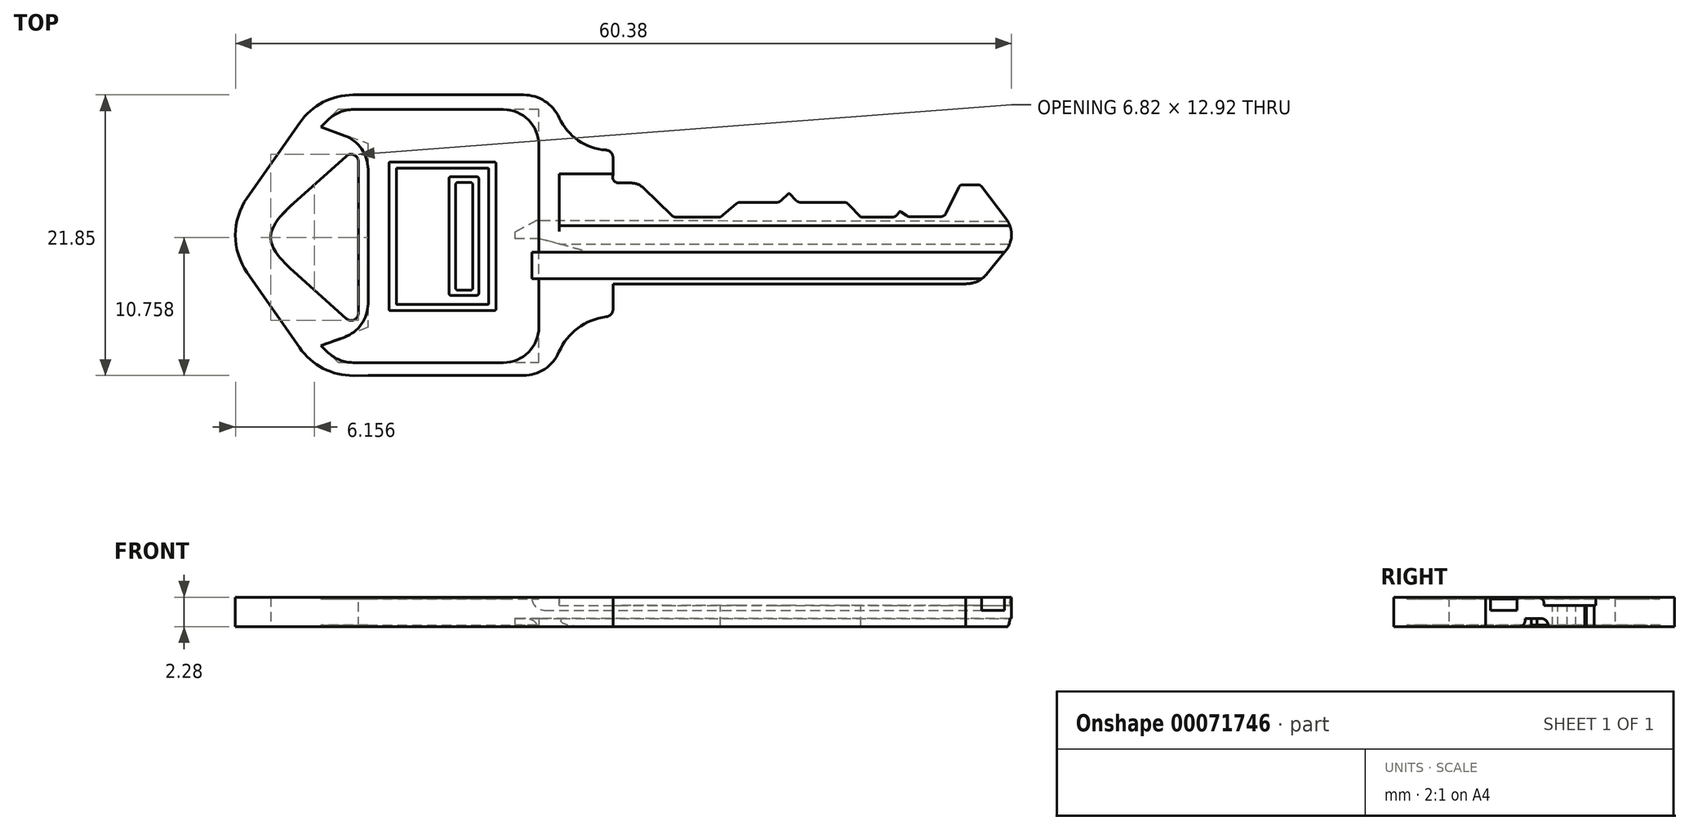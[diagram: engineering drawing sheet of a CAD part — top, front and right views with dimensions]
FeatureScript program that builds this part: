
annotation { "Feature Type Name" : "Feature", "Feature Type Description" : "" }
export const myFeature = defineFeature(function(context is Context, id is Id, definition is map)
    precondition{}
    {
        {
            var Q0;
            Q0=qCreatedBy(makeId("Top.planeOp"),FACE);
            var sketch = newSketch(context, id + "F0", { "sketchPlane" : qUnion([Q0])});
            skLineSegment(sketch, "E0.bottom", {"start": v(-49.06, 40.34) * mm, "end": v(-34.58, 40.34) * mm});
            skLineSegment(sketch, "E0.top", {"start": v(-49.06, 18.5) * mm, "end": v(-34.58, 18.5) * mm});
            skLineSegment(sketch, "E0.left", {"start": v(-49.06, 40.34) * mm, "end": v(-49.06, 18.5) * mm});
            skLineSegment(sketch, "E0.right", {"start": v(-34.58, 40.34) * mm, "end": v(-34.58, 18.5) * mm});
            skLineSegment(sketch, "E1.bottom", {"start": v(-34.58, 33.5) * mm, "end": v(-2.57, 33.5) * mm});
            skLineSegment(sketch, "E1.top", {"start": v(-34.58, 25.63) * mm, "end": v(-2.57, 25.63) * mm});
            skLineSegment(sketch, "E1.left", {"start": v(-34.58, 33.5) * mm, "end": v(-34.58, 25.63) * mm});
            skLineSegment(sketch, "E1.right", {"start": v(-2.57, 33.5) * mm, "end": v(-2.57, 25.63) * mm});
            skLineSegment(sketch, "E2.bottom", {"start": v(-34.58, 36.05) * mm, "end": v(-30, 36.05) * mm});
            skLineSegment(sketch, "E2.top", {"start": v(-34.58, 23.1) * mm, "end": v(-30, 23.1) * mm});
            skLineSegment(sketch, "E2.left", {"start": v(-34.58, 36.05) * mm, "end": v(-34.58, 23.1) * mm});
            skLineSegment(sketch, "E2.right", {"start": v(-30, 36.05) * mm, "end": v(-30, 23.1) * mm});
            skArc(sketch, "E3", {"start": v(-34.58, 40.34) * mm, "mid": v(-33.22, 37.2) * mm, "end": v(-30, 36.05) * mm});
            skArc(sketch, "E4", {"start": v(-30, 23.1) * mm, "mid": v(-33.25, 21.74) * mm, "end": v(-34.58, 18.5) * mm});
            skPoint(sketch, "E5", {"position": v(-30, 33.5) * mm});
            skPoint(sketch, "E6", {"position": v(-30, 25.63) * mm});
            skLineSegment(sketch, "E7", {"start": v(-49.06, 29.42) * mm, "end": v(-2.57, 29.42) * mm});
            skPoint(sketch, "E8", {"position": v(-30, 29.42) * mm});
            skLineSegment(sketch, "E9", {"start": v(-49.06, 40.34) * mm, "end": v(-52.87, 40.34) * mm});
            skLineSegment(sketch, "E10", {"start": v(-52.87, 40.34) * mm, "end": v(-60.5, 29.42) * mm});
            skLineSegment(sketch, "E11", {"start": v(-60.5, 29.42) * mm, "end": v(-52.87, 18.47) * mm});
            skLineSegment(sketch, "E12", {"start": v(-52.87, 18.47) * mm, "end": v(-49.06, 18.5) * mm});
            skLineSegment(sketch, "E13", {"start": v(-2.57, 33.5) * mm, "end": v(-1.57, 33.5) * mm});
            skLineSegment(sketch, "E14", {"start": v(-1.57, 33.5) * mm, "end": v(1.56, 29.42) * mm});
            skLineSegment(sketch, "E15", {"start": v(1.56, 29.42) * mm, "end": v(-1.57, 25.62) * mm});
            skLineSegment(sketch, "E16", {"start": v(-1.57, 25.62) * mm, "end": v(-2.57, 25.63) * mm});
            skSolve(sketch);
        }
        {
            var Q0;
            Q0=makeQuery(id+"F0.imprint","IMPRINT",FACE,{"disambiguationData":[TD([[makeQuery(id+"F0.imprint","IMPRINT",EDGE,{"derivedFrom":sQuery(id+"F0.wireOp",EDGE,"E1.bottom")}),-1.0]])]});
            var Q1;
            {var subQ0=sQuery(id+"F0.wireOp",EDGE,"E3");var subQ3=sQuery(id+"F0.wireOp",EDGE,"E2.bottom");var subQ5=makeQuery(id+"F0.imprint","INTERSECT",VERTEX,{"derivedFrom":[subQ3,subQ0]});Q1=makeQuery(id+"F0.imprint","IMPRINT",FACE,{"disambiguationData":[TD([[makeQuery(id+"F0.imprint","IMPRINT",EDGE,{"disambiguationData":[TD([[subQ5,1.0]])],"derivedFrom":subQ3}),1.0]])]});}
            var Q2;
            {var subQ4=sQuery(id+"F0.wireOp",EDGE,"E1.bottom");var subQ6=sQuery(id+"F0.wireOp",EDGE,"E2.left");var subQ7=makeQuery(id+"F0.imprint","INTERSECT",VERTEX,{"derivedFrom":[subQ4,subQ6]});Q2=makeQuery(id+"F0.imprint","IMPRINT",FACE,{"disambiguationData":[TD([[makeQuery(id+"F0.imprint","IMPRINT",EDGE,{"disambiguationData":[TD([[subQ7,-1.0]])],"derivedFrom":subQ4}),1.0]])]});}
            var Q3;
            {var subQ5=sQuery(id+"F0.wireOp",EDGE,"E2.top");Q3=makeQuery(id+"F0.imprint","IMPRINT",FACE,{"disambiguationData":[TD([[makeQuery(id+"F0.imprint","IMPRINT",EDGE,{"derivedFrom":subQ5}),1.0]])]});}
            var Q4;
            {var subQ0=sQuery(id+"F0.wireOp",EDGE,"E2.top");Q4=makeQuery(id+"F0.imprint","IMPRINT",FACE,{"disambiguationData":[TD([[makeQuery(id+"F0.imprint","IMPRINT",EDGE,{"derivedFrom":subQ0}),-1.0]])]});}
            var Q5;
            {var subQ0=sQuery(id+"F0.wireOp",EDGE,"3a7dfe4d-6823-4ebe-8630-0b1af203f991.3");Q5=makeQuery(id+"F0.imprint","IMPRINT",FACE,{"disambiguationData":[TD([[makeQuery(id+"F0.imprint","IMPRINT",EDGE,{"derivedFrom":subQ0}),1.0]])]});}
            var Q6;
            {var subQ0=sQuery(id+"F0.wireOp",EDGE,"E0.left");Q6=makeQuery(id+"F0.imprint","IMPRINT",FACE,{"disambiguationData":[TD([[makeQuery(id+"F0.imprint","IMPRINT",EDGE,{"derivedFrom":subQ0}),-1.0]])]});}
            var Q7;
            {var subQ4=sQuery(id+"F0.wireOp",EDGE,"E0.left");Q7=makeQuery(id+"F0.imprint","IMPRINT",FACE,{"disambiguationData":[TD([[makeQuery(id+"F0.imprint","IMPRINT",EDGE,{"derivedFrom":subQ4}),1.0]])]});}
            var Q8;
            {var subQ9=sQuery(id+"F0.wireOp",EDGE,"E0.top");Q8=makeQuery(id+"F0.imprint","IMPRINT",FACE,{"disambiguationData":[TD([[makeQuery(id+"F0.imprint","IMPRINT",EDGE,{"derivedFrom":subQ9}),1.0]])]});}
            var Q9;
            {var subQ0=sQuery(id+"F0.wireOp",EDGE,"E2.left");var subQ1=sQuery(id+"F0.wireOp",EDGE,"E1.top");var subQ2=makeQuery(id+"F0.imprint","INTERSECT",VERTEX,{"derivedFrom":[subQ1,subQ0]});Q9=makeQuery(id+"F0.imprint","IMPRINT",FACE,{"disambiguationData":[TD([[makeQuery(id+"F0.imprint","IMPRINT",EDGE,{"disambiguationData":[TD([[subQ2,-1.0]])],"derivedFrom":subQ1}),1.0]])]});}
            var Q10;
            {var subQ0=sQuery(id+"F0.wireOp",EDGE,"E1.right");var subQ1=sQuery(id+"F0.wireOp",EDGE,"E1.top");var subQ2=makeQuery(id+"F0.imprint","INTERSECT",VERTEX,{"derivedFrom":[subQ1,subQ0]});Q10=makeQuery(id+"F0.imprint","IMPRINT",FACE,{"disambiguationData":[TD([[makeQuery(id+"F0.imprint","IMPRINT",EDGE,{"disambiguationData":[TD([[subQ2,1.0]])],"derivedFrom":subQ1}),1.0]])]});}
            var Q11;
            {var subQ3=sQuery(id+"F0.wireOp",EDGE,"E13");Q11=makeQuery(id+"F0.imprint","IMPRINT",FACE,{"disambiguationData":[TD([[makeQuery(id+"F0.imprint","IMPRINT",EDGE,{"derivedFrom":subQ3}),-1.0]])]});}
            extrude(context, id + "F1", {"entities" : qUnion([Q0, Q1, Q2, Q3, Q4, Q5, Q6, Q7, Q8, Q9, Q10, Q11]), "endBound" : BoundingType.SYMMETRIC, "depth" : 2.3 * mm});
        }
        {
            var Q0;
            Q0=makeQuery(id+"F1.opExtrude","CAP_FACE",FACE,{"disambiguationData":[OSD([sQuery(id+"F0.wireOp",EDGE,"E0.bottom"),sQuery(id+"F0.wireOp",EDGE,"E0.top"),sQuery(id+"F0.wireOp",EDGE,"E1.bottom"),sQuery(id+"F0.wireOp",EDGE,"E1.top"),sQuery(id+"F0.wireOp",EDGE,"E1.right"),sQuery(id+"F0.wireOp",EDGE,"E2.right"),sQuery(id+"F0.wireOp",EDGE,"E3"),sQuery(id+"F0.wireOp",EDGE,"E4"),sQuery(id+"F0.wireOp",EDGE,"E9"),sQuery(id+"F0.wireOp",EDGE,"E10"),sQuery(id+"F0.wireOp",EDGE,"E11"),sQuery(id+"F0.wireOp",EDGE,"E12")])],"isStart":false});
            var sketch = newSketch(context, id + "F2", { "sketchPlane" : qUnion([Q0])});
            skLineSegment(sketch, "E17", {"start": v(-57.81, 29.25) * mm, "end": v(-49.81, 22.07) * mm});
            skLineSegment(sketch, "E18", {"start": v(-49.81, 22.07) * mm, "end": v(-49.81, 36.43) * mm});
            skLineSegment(sketch, "E19", {"start": v(-49.81, 36.43) * mm, "end": v(-57.81, 29.25) * mm});
            skPoint(sketch, "E20", {"position": v(-49.81, 29.25) * mm});
            skSolve(sketch);
        }
        {
            var Q0;
            Q0=makeQuery(id+"F1.opExtrude","SWEPT_EDGE",EDGE,{"disambiguationData":[OSD([sQuery(id+"F0.wireOp",EDGE,"E11"),sQuery(id+"F0.wireOp",EDGE,"E12")])]});
            var Q1;
            Q1=makeQuery(id+"F1.opExtrude","SWEPT_EDGE",EDGE,{"disambiguationData":[OSD([sQuery(id+"F0.wireOp",EDGE,"E9"),sQuery(id+"F0.wireOp",EDGE,"E10")])]});
            var Q2;
            Q2=makeQuery(id+"F1.opExtrude","SWEPT_EDGE",EDGE,{"disambiguationData":[OSD([sQuery(id+"F0.wireOp",EDGE,"E10"),sQuery(id+"F0.wireOp",EDGE,"E11")])]});
            fillet(context, id + "F3", {"entities" : qUnion([Q0, Q1, Q2]), "radius" : 5.08 * mm, "tangentPropagation" : true, "allowEdgeOverflow" : false});
        }
        {
            var Q0;
            Q0=makeQuery(id+"F1.opExtrude","SWEPT_EDGE",EDGE,{"disambiguationData":[OSD([sQuery(id+"F0.wireOp",EDGE,"E0.bottom"),sQuery(id+"F0.wireOp",EDGE,"E0.right"),sQuery(id+"F0.wireOp",EDGE,"E3")])]});
            var Q1;
            Q1=makeQuery(id+"F1.opExtrude","SWEPT_EDGE",EDGE,{"disambiguationData":[OSD([sQuery(id+"F0.wireOp",EDGE,"E0.top"),sQuery(id+"F0.wireOp",EDGE,"E0.right"),sQuery(id+"F0.wireOp",EDGE,"E4")])]});
            fillet(context, id + "F4", {"entities" : qUnion([Q0, Q1]), "radius" : 3.05 * mm, "tangentPropagation" : true, "allowEdgeOverflow" : false});
        }
        {
            var Q0;
            Q0=makeQuery(id+"F1.opExtrude","SWEPT_EDGE",EDGE,{"disambiguationData":[OSD([sQuery(id+"F0.wireOp",EDGE,"E2.bottom"),sQuery(id+"F0.wireOp",EDGE,"E2.right"),sQuery(id+"F0.wireOp",EDGE,"E3")])]});
            var Q1;
            Q1=makeQuery(id+"F1.opExtrude","SWEPT_EDGE",EDGE,{"disambiguationData":[OSD([sQuery(id+"F0.wireOp",EDGE,"E2.top"),sQuery(id+"F0.wireOp",EDGE,"E2.right"),sQuery(id+"F0.wireOp",EDGE,"E4")])]});
            fillet(context, id + "F5", {"entities" : qUnion([Q0, Q1]), "radius" : 0.6 * mm, "tangentPropagation" : true, "allowEdgeOverflow" : false});
        }
        {
            var Q0;
            Q0=makeQuery(id+"F2.imprint","IMPRINT",FACE,{"disambiguationData":[TD([[makeQuery(id+"F2.imprint","IMPRINT",EDGE,{"derivedFrom":sQuery(id+"F2.wireOp",EDGE,"E17")}),1.0]])]});
            extrude(context, id + "F6", {"entities" : qUnion([Q0]), "operationType" : NewBodyOperationType.REMOVE, "endBound" : BoundingType.THROUGH_ALL, "oppositeDirection" : true, "depth" : 9.1 * mm});
        }
        {
            var Q0;
            Q0=makeQuery(id+"F6.boolean.opBoolean","COPY",EDGE,{"derivedFrom":makeQuery(id+"F6.opExtrude","SWEPT_EDGE",EDGE,{"disambiguationData":[OSD([sQuery(id+"F2.wireOp",EDGE,"E17"),sQuery(id+"F2.wireOp",EDGE,"E18")])]})});
            var Q1;
            Q1=makeQuery(id+"F6.boolean.opBoolean","COPY",EDGE,{"derivedFrom":makeQuery(id+"F6.opExtrude","SWEPT_EDGE",EDGE,{"disambiguationData":[OSD([sQuery(id+"F2.wireOp",EDGE,"E18"),sQuery(id+"F2.wireOp",EDGE,"E19")])]})});
            fillet(context, id + "F7", {"entities" : qUnion([Q0, Q1]), "radius" : 0.58 * mm, "tangentPropagation" : true, "allowEdgeOverflow" : false});
        }
        {
            var Q0;
            Q0=makeQuery(id+"F6.boolean.opBoolean","COPY",EDGE,{"derivedFrom":makeQuery(id+"F6.opExtrude","SWEPT_EDGE",EDGE,{"disambiguationData":[OSD([sQuery(id+"F2.wireOp",EDGE,"E17"),sQuery(id+"F2.wireOp",EDGE,"E19")])]})});
            fillet(context, id + "F8", {"entities" : qUnion([Q0]), "radius" : 3.55 * mm, "tangentPropagation" : true, "rho" : .6, "crossSection" : FilletCrossSection.CONIC, "allowEdgeOverflow" : false});
        }
        {
            var Q0;
            Q0=makeQuery(id+"F2.imprint","IMPRINT",FACE,{"disambiguationData":[TD([[makeQuery(id+"F2.imprint","IMPRINT",EDGE,{"derivedFrom":sQuery(id+"F2.wireOp",EDGE,"E17")}),-1.0]])]});
            var sketch = newSketch(context, id + "F9", { "sketchPlane" : qUnion([Q0])});
            skLineSegment(sketch, "E21", {"start": v(-49.06, 29.42) * mm, "end": v(-49.06, 36.47) * mm});
            skLineSegment(sketch, "E22", {"start": v(-49.06, 36.47) * mm, "end": v(-52.73, 37.84) * mm});
            skLineSegment(sketch, "E23", {"start": v(-52.73, 37.84) * mm, "end": v(-51.36, 39.2) * mm});
            skLineSegment(sketch, "E24", {"start": v(-51.36, 39.2) * mm, "end": v(-35.77, 39.2) * mm});
            skLineSegment(sketch, "E25", {"start": v(-35.77, 39.2) * mm, "end": v(-35.77, 19.5) * mm});
            skLineSegment(sketch, "E26", {"start": v(-35.77, 19.5) * mm, "end": v(-51.36, 19.5) * mm});
            skLineSegment(sketch, "E27", {"start": v(-51.36, 19.5) * mm, "end": v(-52.73, 20.83) * mm});
            skLineSegment(sketch, "E28", {"start": v(-52.73, 20.83) * mm, "end": v(-49.06, 22.13) * mm});
            skLineSegment(sketch, "E29", {"start": v(-49.06, 22.13) * mm, "end": v(-49.06, 29.42) * mm});
            skLineSegment(sketch, "E30.bottom", {"start": v(-36.33, 28.08) * mm, "end": v(0.92, 28.08) * mm});
            skLineSegment(sketch, "E30.top", {"start": v(-36.33, 26.03) * mm, "end": v(0.92, 26.03) * mm});
            skLineSegment(sketch, "E30.left", {"start": v(-36.33, 28.08) * mm, "end": v(-36.33, 26.03) * mm});
            skLineSegment(sketch, "E30.right", {"start": v(0.92, 28.08) * mm, "end": v(0.92, 26.03) * mm});
            skLineSegment(sketch, "E31.bottom", {"start": v(-34.2, 34.2) * mm, "end": v(3.04, 34.2) * mm});
            skLineSegment(sketch, "E31.top", {"start": v(-34.2, 30.17) * mm, "end": v(3.04, 30.17) * mm});
            skLineSegment(sketch, "E31.left", {"start": v(-34.2, 34.2) * mm, "end": v(-34.2, 30.17) * mm});
            skLineSegment(sketch, "E31.right", {"start": v(3.04, 34.2) * mm, "end": v(3.04, 30.17) * mm});
            skSolve(sketch);
        }
        {
            var Q0;
            Q0=makeQuery(id+"F1.opExtrude","CAP_FACE",FACE,{"disambiguationData":[OSD([sQuery(id+"F0.wireOp",EDGE,"E0.bottom"),sQuery(id+"F0.wireOp",EDGE,"E0.top"),sQuery(id+"F0.wireOp",EDGE,"E1.bottom"),sQuery(id+"F0.wireOp",EDGE,"E1.top"),sQuery(id+"F0.wireOp",EDGE,"E2.right"),sQuery(id+"F0.wireOp",EDGE,"E3"),sQuery(id+"F0.wireOp",EDGE,"E4"),sQuery(id+"F0.wireOp",EDGE,"E9"),sQuery(id+"F0.wireOp",EDGE,"E10"),sQuery(id+"F0.wireOp",EDGE,"E11"),sQuery(id+"F0.wireOp",EDGE,"E12"),sQuery(id+"F0.wireOp",EDGE,"E13"),sQuery(id+"F0.wireOp",EDGE,"E14"),sQuery(id+"F0.wireOp",EDGE,"E15"),sQuery(id+"F0.wireOp",EDGE,"E16")])],"isStart":true});
            var sketch = newSketch(context, id + "F10", { "sketchPlane" : qUnion([Q0])});
            skLineSegment(sketch, "E32", {"start": v(-49.08, -22.24) * mm, "end": v(-49.08, -19.13) * mm});
            skLineSegment(sketch, "E33", {"start": v(-49.08, -22.24) * mm, "end": v(-52.74, -20.87) * mm});
            skLineSegment(sketch, "E34", {"start": v(-52.74, -20.87) * mm, "end": v(-51.38, -19.51) * mm});
            skLineSegment(sketch, "E35", {"start": v(-51.38, -19.51) * mm, "end": v(-35.78, -19.51) * mm});
            skLineSegment(sketch, "E36", {"start": v(-35.78, -19.51) * mm, "end": v(-35.78, -39.2) * mm});
            skLineSegment(sketch, "E37", {"start": v(-35.78, -39.2) * mm, "end": v(-51.38, -39.2) * mm});
            skLineSegment(sketch, "E38", {"start": v(-51.38, -39.2) * mm, "end": v(-52.74, -37.88) * mm});
            skLineSegment(sketch, "E39", {"start": v(-52.74, -37.88) * mm, "end": v(-49.08, -36.58) * mm});
            skLineSegment(sketch, "E40", {"start": v(-49.08, -36.58) * mm, "end": v(-49.08, -19.13) * mm});
            skLineSegment(sketch, "E41", {"start": v(-35.64, -30.58) * mm, "end": v(-35.92, -30.58) * mm});
            skLineSegment(sketch, "E42", {"start": v(-35.92, -30.58) * mm, "end": v(-37.64, -29.65) * mm});
            skLineSegment(sketch, "E43", {"start": v(-37.64, -29.65) * mm, "end": v(-37.64, -29.19) * mm});
            skLineSegment(sketch, "E44", {"start": v(-37.64, -29.19) * mm, "end": v(-35.78, -29.19) * mm});
            skLineSegment(sketch, "E45", {"start": v(-35.78, -29.19) * mm, "end": v(-34.07, -28.7) * mm});
            skLineSegment(sketch, "E46", {"start": v(-34.07, -28.7) * mm, "end": v(2.33, -28.7) * mm});
            skLineSegment(sketch, "E47", {"start": v(2.33, -28.7) * mm, "end": v(2.33, -30.5) * mm});
            skLineSegment(sketch, "E48", {"start": v(2.33, -30.5) * mm, "end": v(-35.64, -30.58) * mm});
            skSolve(sketch);
        }
        {
            var Q0;
            Q0=makeQuery(id+"F9.imprint","IMPRINT",FACE,{"disambiguationData":[TD([[makeQuery(id+"F9.imprint","IMPRINT",EDGE,{"derivedFrom":sQuery(id+"F9.wireOp",EDGE,"E21")}),-1.0]])]});
            var Q1;
            {var subQ4=sQuery(id+"F10.wireOp",EDGE,"E37");Q1=makeQuery(id+"F10.imprint","IMPRINT",FACE,{"disambiguationData":[TD([[makeQuery(id+"F10.imprint","IMPRINT",EDGE,{"derivedFrom":subQ4}),-1.0]])]});}
            var Q2;
            {var subQ0=sQuery(id+"F10.wireOp",EDGE,"E33");Q2=makeQuery(id+"F10.imprint","IMPRINT",FACE,{"disambiguationData":[TD([[makeQuery(id+"F10.imprint","IMPRINT",EDGE,{"derivedFrom":subQ0}),-1.0]])]});}
            extrude(context, id + "F11", {"entities" : qUnion([Q0, Q1, Q2]), "operationType" : NewBodyOperationType.REMOVE, "endBound" : BoundingType.SYMMETRIC, "oppositeDirection" : true, "depth" : 0.25 * mm});
        }
        {
            var Q0;
            Q0=makeQuery(id+"F11.boolean.opBoolean","COPY",EDGE,{"derivedFrom":makeQuery(id+"F11.opExtrude","SWEPT_EDGE",EDGE,{"disambiguationData":[OSD([sQuery(id+"F9.wireOp",EDGE,"E28"),sQuery(id+"F9.wireOp",EDGE,"E29")])]})});
            var Q1;
            Q1=makeQuery(id+"F11.boolean.opBoolean","COPY",EDGE,{"derivedFrom":makeQuery(id+"F11.opExtrude","SWEPT_EDGE",EDGE,{"disambiguationData":[OSD([sQuery(id+"F9.wireOp",EDGE,"E21"),sQuery(id+"F9.wireOp",EDGE,"E22")])]})});
            var Q2;
            Q2=makeQuery(id+"F11.boolean.opBoolean","COPY",EDGE,{"derivedFrom":makeQuery(id+"F11.opExtrude","SWEPT_EDGE",EDGE,{"disambiguationData":[OSD([sQuery(id+"F9.wireOp",EDGE,"E25"),sQuery(id+"F9.wireOp",EDGE,"E26")])]})});
            var Q3;
            Q3=makeQuery(id+"F11.boolean.opBoolean","COPY",EDGE,{"derivedFrom":makeQuery(id+"F11.opExtrude","SWEPT_EDGE",EDGE,{"disambiguationData":[OSD([sQuery(id+"F9.wireOp",EDGE,"E24"),sQuery(id+"F9.wireOp",EDGE,"E25")])]})});
            var Q4;
            Q4=makeQuery(id+"F11.boolean.opBoolean","COPY",EDGE,{"derivedFrom":makeQuery(id+"F11.opExtrude","SWEPT_EDGE",EDGE,{"disambiguationData":[OSD([sQuery(id+"F9.wireOp",EDGE,"E26"),sQuery(id+"F9.wireOp",EDGE,"E27")])]})});
            var Q5;
            Q5=makeQuery(id+"F11.boolean.opBoolean","COPY",EDGE,{"derivedFrom":makeQuery(id+"F11.opExtrude","SWEPT_EDGE",EDGE,{"disambiguationData":[OSD([sQuery(id+"F9.wireOp",EDGE,"E23"),sQuery(id+"F9.wireOp",EDGE,"E24")])]})});
            fillet(context, id + "F12", {"entities" : qUnion([Q0, Q1, Q2, Q3, Q4, Q5]), "radius" : 2.8 * mm, "tangentPropagation" : true, "allowEdgeOverflow" : false});
        }
        {
            var Q0;
            Q0=makeQuery(id+"F1.opExtrude","SWEPT_EDGE",EDGE,{"disambiguationData":[OSD([sQuery(id+"F0.wireOp",EDGE,"E15"),sQuery(id+"F0.wireOp",EDGE,"E16")])]});
            var Q1;
            Q1=makeQuery(id+"F1.opExtrude","SWEPT_EDGE",EDGE,{"disambiguationData":[OSD([sQuery(id+"F0.wireOp",EDGE,"E14"),sQuery(id+"F0.wireOp",EDGE,"E15")])]});
            fillet(context, id + "F13", {"entities" : qUnion([Q0, Q1]), "radius" : 2.05 * mm, "tangentPropagation" : true, "allowEdgeOverflow" : false});
        }
        {
            var Q0;
            {var subQ1=sQuery(id+"F9.wireOp",EDGE,"E31.top");Q0=makeQuery(id+"F9.imprint","IMPRINT",FACE,{"disambiguationData":[TD([[makeQuery(id+"F9.imprint","IMPRINT",EDGE,{"derivedFrom":subQ1}),1.0]])]});}
            extrude(context, id + "F14", {"entities" : qUnion([Q0]), "operationType" : NewBodyOperationType.REMOVE, "endBound" : BoundingType.SYMMETRIC, "oppositeDirection" : true, "depth" : 1.27 * mm});
        }
        {
            var Q0;
            {var subQ4=sQuery(id+"F10.wireOp",EDGE,"E42");Q0=makeQuery(id+"F10.imprint","IMPRINT",FACE,{"disambiguationData":[TD([[makeQuery(id+"F10.imprint","IMPRINT",EDGE,{"derivedFrom":subQ4}),-1.0]])]});}
            var Q1;
            {var subQ1=sQuery(id+"F10.wireOp",EDGE,"E45");Q1=makeQuery(id+"F10.imprint","IMPRINT",FACE,{"disambiguationData":[TD([[makeQuery(id+"F10.imprint","IMPRINT",EDGE,{"derivedFrom":subQ1}),-1.0]])]});}
            extrude(context, id + "F15", {"entities" : qUnion([Q0, Q1]), "operationType" : NewBodyOperationType.REMOVE, "endBound" : BoundingType.SYMMETRIC, "oppositeDirection" : true, "depth" : 1.27 * mm});
        }
        {
            var Q0;
            {var subQ0=sQuery(id+"F9.wireOp",EDGE,"E30.bottom");var subQ1=sQuery(id+"F9.wireOp",EDGE,"E25");var subQ2=makeQuery(id+"F9.imprint","INTERSECT",VERTEX,{"derivedFrom":[subQ1,subQ0]});Q0=makeQuery(id+"F9.imprint","IMPRINT",FACE,{"disambiguationData":[TD([[makeQuery(id+"F9.imprint","IMPRINT",EDGE,{"disambiguationData":[TD([[subQ2,-1.0]])],"derivedFrom":subQ1}),1.0]])]});}
            var Q1;
            {var subQ5=sQuery(id+"F9.wireOp",EDGE,"E30.left");Q1=makeQuery(id+"F9.imprint","IMPRINT",FACE,{"disambiguationData":[TD([[makeQuery(id+"F9.imprint","IMPRINT",EDGE,{"derivedFrom":subQ5}),1.0]])]});}
            var Q2;
            {var subQ0=sQuery(id+"F9.wireOp",EDGE,"E30.right");Q2=makeQuery(id+"F9.imprint","IMPRINT",FACE,{"disambiguationData":[TD([[makeQuery(id+"F9.imprint","IMPRINT",EDGE,{"derivedFrom":subQ0}),-1.0]])]});}
            extrude(context, id + "F16", {"entities" : qUnion([Q0, Q1, Q2]), "operationType" : NewBodyOperationType.REMOVE, "endBound" : BoundingType.SYMMETRIC, "oppositeDirection" : true, "depth" : 2.03 * mm});
        }
        {
            var Q0;
            Q0=makeQuery(id+"F16.boolean.opBoolean","COPY",EDGE,{"derivedFrom":makeQuery(id+"F16.opExtrude","CAP_EDGE",EDGE,{"disambiguationData":[OSD([sQuery(id+"F9.wireOp",EDGE,"E30.left")])],"isStart":false})});
            fillet(context, id + "F17", {"entities" : qUnion([Q0]), "radius" : 0.99 * mm, "tangentPropagation" : true, "allowEdgeOverflow" : false});
        }
        {
            var Q0;
            Q0=makeQuery(id+"F14.boolean.opBoolean","INTERSECT",EDGE,{"derivedFrom":[makeQuery(id+"F1.opExtrude","CAP_FACE",FACE,{"disambiguationData":[OSD([sQuery(id+"F0.wireOp",EDGE,"E0.bottom"),sQuery(id+"F0.wireOp",EDGE,"E0.top"),sQuery(id+"F0.wireOp",EDGE,"E1.bottom"),sQuery(id+"F0.wireOp",EDGE,"E1.top"),sQuery(id+"F0.wireOp",EDGE,"E2.right"),sQuery(id+"F0.wireOp",EDGE,"E3"),sQuery(id+"F0.wireOp",EDGE,"E4"),sQuery(id+"F0.wireOp",EDGE,"E9"),sQuery(id+"F0.wireOp",EDGE,"E10"),sQuery(id+"F0.wireOp",EDGE,"E11"),sQuery(id+"F0.wireOp",EDGE,"E12"),sQuery(id+"F0.wireOp",EDGE,"E13"),sQuery(id+"F0.wireOp",EDGE,"E14"),sQuery(id+"F0.wireOp",EDGE,"E15"),sQuery(id+"F0.wireOp",EDGE,"E16")])],"isStart":false}),makeQuery(id+"F14.opExtrude","SWEPT_FACE",FACE,{"disambiguationData":[OSD([sQuery(id+"F9.wireOp",EDGE,"E31.top")])]})]});
            var Q1;
            Q1=makeQuery(id+"F15.boolean.opBoolean","INTERSECT",EDGE,{"derivedFrom":[makeQuery(id+"F1.opExtrude","CAP_FACE",FACE,{"disambiguationData":[OSD([sQuery(id+"F0.wireOp",EDGE,"E0.bottom"),sQuery(id+"F0.wireOp",EDGE,"E0.top"),sQuery(id+"F0.wireOp",EDGE,"E1.bottom"),sQuery(id+"F0.wireOp",EDGE,"E1.top"),sQuery(id+"F0.wireOp",EDGE,"E2.right"),sQuery(id+"F0.wireOp",EDGE,"E3"),sQuery(id+"F0.wireOp",EDGE,"E4"),sQuery(id+"F0.wireOp",EDGE,"E9"),sQuery(id+"F0.wireOp",EDGE,"E10"),sQuery(id+"F0.wireOp",EDGE,"E11"),sQuery(id+"F0.wireOp",EDGE,"E12"),sQuery(id+"F0.wireOp",EDGE,"E13"),sQuery(id+"F0.wireOp",EDGE,"E14"),sQuery(id+"F0.wireOp",EDGE,"E15"),sQuery(id+"F0.wireOp",EDGE,"E16")])],"isStart":true}),makeQuery(id+"F15.opExtrude","SWEPT_FACE",FACE,{"disambiguationData":[OSD([sQuery(id+"F10.wireOp",EDGE,"E46")])]})]});
            fillet(context, id + "F18", {"entities" : qUnion([Q0, Q1]), "radius" : 0.47 * mm, "tangentPropagation" : true, "allowEdgeOverflow" : false});
        }
        {
            var Q0;
            Q0=makeQuery(id+"F2.imprint","IMPRINT",FACE,{"disambiguationData":[TD([[makeQuery(id+"F2.imprint","IMPRINT",EDGE,{"derivedFrom":sQuery(id+"F2.wireOp",EDGE,"E17")}),-1.0]])]});
            var sketch = newSketch(context, id + "F19", { "sketchPlane" : qUnion([Q0])});
            skLineSegment(sketch, "E49", {"start": v(-1.26, 33.34) * mm, "end": v(-3, 33.34) * mm});
            skLineSegment(sketch, "E50", {"start": v(-3, 33.34) * mm, "end": v(-4.22, 30.86) * mm});
            skLineSegment(sketch, "E51", {"start": v(-4.22, 30.86) * mm, "end": v(-7.06, 30.86) * mm});
            skLineSegment(sketch, "E52", {"start": v(-7.06, 30.86) * mm, "end": v(-7.7, 31.3) * mm});
            skLineSegment(sketch, "E53", {"start": v(-7.7, 31.3) * mm, "end": v(-8.02, 30.83) * mm});
            skLineSegment(sketch, "E54", {"start": v(-8.02, 30.83) * mm, "end": v(-10.72, 30.83) * mm});
            skLineSegment(sketch, "E55", {"start": v(-10.72, 30.83) * mm, "end": v(-11.82, 31.97) * mm});
            skLineSegment(sketch, "E56", {"start": v(-11.82, 31.97) * mm, "end": v(-15.61, 31.97) * mm});
            skLineSegment(sketch, "E57", {"start": v(-15.61, 31.97) * mm, "end": v(-16.3, 32.7) * mm});
            skLineSegment(sketch, "E58", {"start": v(-16.3, 32.7) * mm, "end": v(-17.07, 31.97) * mm});
            skLineSegment(sketch, "E59", {"start": v(-17.07, 31.97) * mm, "end": v(-20.29, 31.97) * mm});
            skLineSegment(sketch, "E60", {"start": v(-20.29, 31.97) * mm, "end": v(-21.65, 30.83) * mm});
            skLineSegment(sketch, "E61", {"start": v(-21.65, 30.83) * mm, "end": v(-25.31, 30.83) * mm});
            skLineSegment(sketch, "E62", {"start": v(-25.31, 30.83) * mm, "end": v(-28.03, 33.48) * mm});
            skLineSegment(sketch, "E63", {"start": v(-28.03, 33.48) * mm, "end": v(-30.03, 33.48) * mm});
            skLineSegment(sketch, "E64", {"start": v(-30.03, 33.48) * mm, "end": v(-30.03, 34.07) * mm});
            skLineSegment(sketch, "E65", {"start": v(-30.03, 34.07) * mm, "end": v(-1.31, 34.07) * mm});
            skLineSegment(sketch, "E66", {"start": v(-1.31, 34.07) * mm, "end": v(-1.26, 33.34) * mm});
            skSolve(sketch);
        }
        {
            var Q0;
            Q0 = qSketchRegion(id + "F19", true);
            extrude(context, id + "F20", {"entities" : qUnion([Q0]), "operationType" : NewBodyOperationType.REMOVE, "endBound" : BoundingType.THROUGH_ALL, "oppositeDirection" : true, "depth" : 25.4 * mm});
        }
        {
            var Q0;
            Q0=makeQuery(id+"F20.boolean.opBoolean","COPY",EDGE,{"derivedFrom":makeQuery(id+"F20.opExtrude","SWEPT_EDGE",EDGE,{"disambiguationData":[OSD([sQuery(id+"F19.wireOp",EDGE,"E63"),sQuery(id+"F19.wireOp",EDGE,"E64")])]})});
            var Q1;
            Q1=makeQuery(id+"F20.boolean.opBoolean","COPY",EDGE,{"derivedFrom":makeQuery(id+"F20.opExtrude","SWEPT_EDGE",EDGE,{"disambiguationData":[OSD([sQuery(id+"F19.wireOp",EDGE,"E59"),sQuery(id+"F19.wireOp",EDGE,"E60")])]})});
            var Q2;
            Q2=makeQuery(id+"F20.boolean.opBoolean","COPY",EDGE,{"derivedFrom":makeQuery(id+"F20.opExtrude","SWEPT_EDGE",EDGE,{"disambiguationData":[OSD([sQuery(id+"F19.wireOp",EDGE,"E55"),sQuery(id+"F19.wireOp",EDGE,"E56")])]})});
            var Q3;
            Q3=makeQuery(id+"F20.boolean.opBoolean","COPY",EDGE,{"derivedFrom":makeQuery(id+"F20.opExtrude","SWEPT_EDGE",EDGE,{"disambiguationData":[OSD([sQuery(id+"F19.wireOp",EDGE,"E51"),sQuery(id+"F19.wireOp",EDGE,"E52")])]})});
            var Q4;
            Q4=makeQuery(id+"F20.boolean.opBoolean","COPY",EDGE,{"derivedFrom":makeQuery(id+"F20.opExtrude","SWEPT_EDGE",EDGE,{"disambiguationData":[OSD([sQuery(id+"F19.wireOp",EDGE,"E53"),sQuery(id+"F19.wireOp",EDGE,"E54")])]})});
            var Q5;
            Q5=makeQuery(id+"F20.boolean.opBoolean","COPY",EDGE,{"derivedFrom":makeQuery(id+"F20.opExtrude","SWEPT_EDGE",EDGE,{"disambiguationData":[OSD([sQuery(id+"F19.wireOp",EDGE,"E50"),sQuery(id+"F19.wireOp",EDGE,"E51")])]})});
            var Q6;
            Q6=makeQuery(id+"F20.boolean.opBoolean","COPY",EDGE,{"derivedFrom":makeQuery(id+"F20.opExtrude","SWEPT_EDGE",EDGE,{"disambiguationData":[OSD([sQuery(id+"F19.wireOp",EDGE,"E58"),sQuery(id+"F19.wireOp",EDGE,"E59")])]})});
            var Q7;
            Q7=makeQuery(id+"F20.boolean.opBoolean","COPY",EDGE,{"derivedFrom":makeQuery(id+"F20.opExtrude","SWEPT_EDGE",EDGE,{"disambiguationData":[OSD([sQuery(id+"F19.wireOp",EDGE,"E56"),sQuery(id+"F19.wireOp",EDGE,"E57")])]})});
            var Q8;
            Q8=makeQuery(id+"F20.boolean.opBoolean","COPY",EDGE,{"derivedFrom":makeQuery(id+"F20.opExtrude","SWEPT_EDGE",EDGE,{"disambiguationData":[OSD([sQuery(id+"F19.wireOp",EDGE,"E61"),sQuery(id+"F19.wireOp",EDGE,"E62")])]})});
            fillet(context, id + "F21", {"entities" : qUnion([Q0, Q1, Q2, Q3, Q4, Q5, Q6, Q7, Q8]), "radius" : 0.5 * mm, "tangentPropagation" : true, "allowEdgeOverflow" : false});
        }
        {
            var Q0;
            Q0=makeQuery(id+"F20.boolean.opBoolean","COPY",EDGE,{"derivedFrom":makeQuery(id+"F20.opExtrude","SWEPT_EDGE",EDGE,{"disambiguationData":[OSD([sQuery(id+"F19.wireOp",EDGE,"E62"),sQuery(id+"F19.wireOp",EDGE,"E63")])]})});
            fillet(context, id + "F22", {"entities" : qUnion([Q0]), "radius" : 1.4 * mm, "tangentPropagation" : true, "allowEdgeOverflow" : false});
        }
        {
            var Q0;
            Q0=makeQuery(id+"F20.boolean.opBoolean","COPY",EDGE,{"derivedFrom":makeQuery(id+"F20.opExtrude","SWEPT_EDGE",EDGE,{"disambiguationData":[OSD([sQuery(id+"F19.wireOp",EDGE,"E49"),sQuery(id+"F19.wireOp",EDGE,"E50")])]})});
            var Q1;
            Q1=makeQuery(id+"F20.boolean.opBoolean","INTERSECT",EDGE,{"derivedFrom":[makeQuery(id+"F1.opExtrude","SWEPT_FACE",FACE,{"disambiguationData":[OSD([sQuery(id+"F0.wireOp",EDGE,"E14")])]}),makeQuery(id+"F20.opExtrude","SWEPT_FACE",FACE,{"disambiguationData":[OSD([sQuery(id+"F19.wireOp",EDGE,"E49")])]})]});
            fillet(context, id + "F23", {"entities" : qUnion([Q0, Q1]), "radius" : 0.36 * mm, "tangentPropagation" : true, "allowEdgeOverflow" : false});
        }
        {
            var Q0;
            Q0=makeQuery(id+"F20.boolean.opBoolean","COPY",EDGE,{"derivedFrom":makeQuery(id+"F20.opExtrude","SWEPT_EDGE",EDGE,{"disambiguationData":[OSD([sQuery(id+"F19.wireOp",EDGE,"E52"),sQuery(id+"F19.wireOp",EDGE,"E53")])]})});
            var Q1;
            Q1=makeQuery(id+"F20.boolean.opBoolean","COPY",EDGE,{"derivedFrom":makeQuery(id+"F20.opExtrude","SWEPT_EDGE",EDGE,{"disambiguationData":[OSD([sQuery(id+"F19.wireOp",EDGE,"E57"),sQuery(id+"F19.wireOp",EDGE,"E58")])]})});
            fillet(context, id + "F24", {"entities" : qUnion([Q0, Q1]), "radius" : 0.1 * mm, "tangentPropagation" : true, "allowEdgeOverflow" : false});
        }
        {
            var Q0;
            Q0=makeQuery(id+"F15.boolean.opBoolean","COPY",EDGE,{"derivedFrom":makeQuery(id+"F15.opExtrude","CAP_EDGE",EDGE,{"disambiguationData":[OSD([sQuery(id+"F10.wireOp",EDGE,"E48")])],"isStart":false})});
            fillet(context, id + "F25", {"entities" : qUnion([Q0]), "radius" : 0.58 * mm, "tangentPropagation" : true, "allowEdgeOverflow" : false});
        }
        {
            var Q0;
            Q0=makeQuery(id+"F9.imprint","IMPRINT",FACE,{"disambiguationData":[TD([[makeQuery(id+"F9.imprint","IMPRINT",EDGE,{"derivedFrom":sQuery(id+"F9.wireOp",EDGE,"E21")}),-1.0]])]});
            var sketch = newSketch(context, id + "F26", { "sketchPlane" : qUnion([Q0])});
            skLineSegment(sketch, "E67.bottom", {"start": v(-47.44, 23.56) * mm, "end": v(-39.12, 23.56) * mm});
            skLineSegment(sketch, "E67.top", {"start": v(-47.44, 35.1) * mm, "end": v(-39.12, 35.1) * mm});
            skLineSegment(sketch, "E67.left", {"start": v(-47.44, 23.56) * mm, "end": v(-47.44, 35.1) * mm});
            skLineSegment(sketch, "E67.right", {"start": v(-39.12, 23.56) * mm, "end": v(-39.12, 35.1) * mm});
            skLineSegment(sketch, "E68.bottom", {"start": v(-46.87, 24.02) * mm, "end": v(-39.69, 24.02) * mm});
            skLineSegment(sketch, "E68.top", {"start": v(-46.87, 34.64) * mm, "end": v(-39.69, 34.64) * mm});
            skLineSegment(sketch, "E68.left", {"start": v(-46.87, 24.02) * mm, "end": v(-46.87, 34.64) * mm});
            skLineSegment(sketch, "E68.right", {"start": v(-39.69, 24.02) * mm, "end": v(-39.69, 34.64) * mm});
            skLineSegment(sketch, "E69.bottom", {"start": v(-42.77, 24.74) * mm, "end": v(-40.46, 24.74) * mm});
            skLineSegment(sketch, "E69.top", {"start": v(-42.77, 33.97) * mm, "end": v(-40.46, 33.97) * mm});
            skLineSegment(sketch, "E69.left", {"start": v(-42.77, 24.74) * mm, "end": v(-42.77, 33.97) * mm});
            skLineSegment(sketch, "E69.right", {"start": v(-40.46, 24.74) * mm, "end": v(-40.46, 33.97) * mm});
            skLineSegment(sketch, "E70.bottom", {"start": v(-42.25, 25.15) * mm, "end": v(-40.92, 25.15) * mm});
            skLineSegment(sketch, "E70.top", {"start": v(-42.25, 33.51) * mm, "end": v(-40.92, 33.51) * mm});
            skLineSegment(sketch, "E70.left", {"start": v(-42.25, 25.15) * mm, "end": v(-42.25, 33.51) * mm});
            skLineSegment(sketch, "E70.right", {"start": v(-40.92, 25.15) * mm, "end": v(-40.92, 33.51) * mm});
            skSolve(sketch);
        }
        {
            var Q0;
            Q0 = qSketchRegion(id + "F26", true);
            var Q1;
            Q1=makeQuery(id+"F26.imprint","IMPRINT",FACE,{"disambiguationData":[TD([[makeQuery(id+"F26.imprint","IMPRINT",EDGE,{"derivedFrom":sQuery(id+"F26.wireOp",EDGE,"E69.bottom")}),1.0]])]});
            var Q2;
            Q2=makeQuery(id+"F11.boolean.opBoolean","COPY",FACE,{"derivedFrom":makeQuery(id+"F11.opExtrude","CAP_FACE",FACE,{"disambiguationData":[OSD([sQuery(id+"F9.wireOp",EDGE,"E21"),sQuery(id+"F9.wireOp",EDGE,"E22"),sQuery(id+"F9.wireOp",EDGE,"E23"),sQuery(id+"F9.wireOp",EDGE,"E24"),sQuery(id+"F9.wireOp",EDGE,"E25"),sQuery(id+"F9.wireOp",EDGE,"E26"),sQuery(id+"F9.wireOp",EDGE,"E27"),sQuery(id+"F9.wireOp",EDGE,"E28"),sQuery(id+"F9.wireOp",EDGE,"E29"),sQuery(id+"F9.wireOp",EDGE,"E30.bottom"),sQuery(id+"F9.wireOp",EDGE,"E30.top"),sQuery(id+"F9.wireOp",EDGE,"E30.left")])],"isStart":false})});
            extrude(context, id + "F27", {"entities" : qUnion([Q0, Q1]), "operationType" : NewBodyOperationType.ADD, "endBound" : BoundingType.UP_TO_SURFACE, "oppositeDirection" : true, "endBoundEntityFace" : qUnion([Q2]), "depth" : 0.15 * mm});
        }
        {
            var Q0;
            Q0=makeQuery(id+"F27.opExtrude","SWEPT_EDGE",EDGE,{"disambiguationData":[OSD([sQuery(id+"F26.wireOp",EDGE,"E67.bottom"),sQuery(id+"F26.wireOp",EDGE,"E67.left")])]});
            var Q1;
            Q1=makeQuery(id+"F27.opExtrude","SWEPT_EDGE",EDGE,{"disambiguationData":[OSD([sQuery(id+"F26.wireOp",EDGE,"E67.top"),sQuery(id+"F26.wireOp",EDGE,"E67.left")])]});
            var Q2;
            Q2=makeQuery(id+"F27.opExtrude","SWEPT_EDGE",EDGE,{"disambiguationData":[OSD([sQuery(id+"F26.wireOp",EDGE,"E67.top"),sQuery(id+"F26.wireOp",EDGE,"E67.right")])]});
            var Q3;
            Q3=makeQuery(id+"F27.opExtrude","SWEPT_EDGE",EDGE,{"disambiguationData":[OSD([sQuery(id+"F26.wireOp",EDGE,"E67.bottom"),sQuery(id+"F26.wireOp",EDGE,"E67.right")])]});
            var Q4;
            Q4=makeQuery(id+"F27.opExtrude","SWEPT_EDGE",EDGE,{"disambiguationData":[OSD([sQuery(id+"F26.wireOp",EDGE,"E68.bottom"),sQuery(id+"F26.wireOp",EDGE,"E68.right")])]});
            var Q5;
            Q5=makeQuery(id+"F27.opExtrude","SWEPT_EDGE",EDGE,{"disambiguationData":[OSD([sQuery(id+"F26.wireOp",EDGE,"E68.bottom"),sQuery(id+"F26.wireOp",EDGE,"E68.left")])]});
            var Q6;
            Q6=makeQuery(id+"F27.opExtrude","SWEPT_EDGE",EDGE,{"disambiguationData":[OSD([sQuery(id+"F26.wireOp",EDGE,"E68.top"),sQuery(id+"F26.wireOp",EDGE,"E68.left")])]});
            var Q7;
            Q7=makeQuery(id+"F27.opExtrude","SWEPT_EDGE",EDGE,{"disambiguationData":[OSD([sQuery(id+"F26.wireOp",EDGE,"E68.top"),sQuery(id+"F26.wireOp",EDGE,"E68.right")])]});
            fillet(context, id + "F28", {"entities" : qUnion([Q0, Q1, Q2, Q3, Q4, Q5, Q6, Q7]), "radius" : 0.08 * mm, "tangentPropagation" : true, "allowEdgeOverflow" : false});
        }
        {
            var Q0;
            Q0=makeQuery(id+"F27.opExtrude","SWEPT_EDGE",EDGE,{"disambiguationData":[OSD([sQuery(id+"F26.wireOp",EDGE,"E69.top"),sQuery(id+"F26.wireOp",EDGE,"E69.right")])]});
            var Q1;
            Q1=makeQuery(id+"F27.opExtrude","SWEPT_EDGE",EDGE,{"disambiguationData":[OSD([sQuery(id+"F26.wireOp",EDGE,"E70.top"),sQuery(id+"F26.wireOp",EDGE,"E70.right")])]});
            var Q2;
            Q2=makeQuery(id+"F27.opExtrude","SWEPT_EDGE",EDGE,{"disambiguationData":[OSD([sQuery(id+"F26.wireOp",EDGE,"E69.top"),sQuery(id+"F26.wireOp",EDGE,"E69.left")])]});
            var Q3;
            Q3=makeQuery(id+"F27.opExtrude","SWEPT_EDGE",EDGE,{"disambiguationData":[OSD([sQuery(id+"F26.wireOp",EDGE,"E70.top"),sQuery(id+"F26.wireOp",EDGE,"E70.left")])]});
            var Q4;
            Q4=makeQuery(id+"F27.opExtrude","SWEPT_EDGE",EDGE,{"disambiguationData":[OSD([sQuery(id+"F26.wireOp",EDGE,"E69.bottom"),sQuery(id+"F26.wireOp",EDGE,"E69.left")])]});
            var Q5;
            Q5=makeQuery(id+"F27.opExtrude","SWEPT_EDGE",EDGE,{"disambiguationData":[OSD([sQuery(id+"F26.wireOp",EDGE,"E69.bottom"),sQuery(id+"F26.wireOp",EDGE,"E69.right")])]});
            var Q6;
            Q6=makeQuery(id+"F27.opExtrude","SWEPT_EDGE",EDGE,{"disambiguationData":[OSD([sQuery(id+"F26.wireOp",EDGE,"E70.bottom"),sQuery(id+"F26.wireOp",EDGE,"E70.left")])]});
            var Q7;
            Q7=makeQuery(id+"F27.opExtrude","SWEPT_EDGE",EDGE,{"disambiguationData":[OSD([sQuery(id+"F26.wireOp",EDGE,"E70.bottom"),sQuery(id+"F26.wireOp",EDGE,"E70.right")])]});
            fillet(context, id + "F29", {"entities" : qUnion([Q0, Q1, Q2, Q3, Q4, Q5, Q6, Q7]), "radius" : 0.15 * mm, "tangentPropagation" : true, "allowEdgeOverflow" : false});
        }
    });
